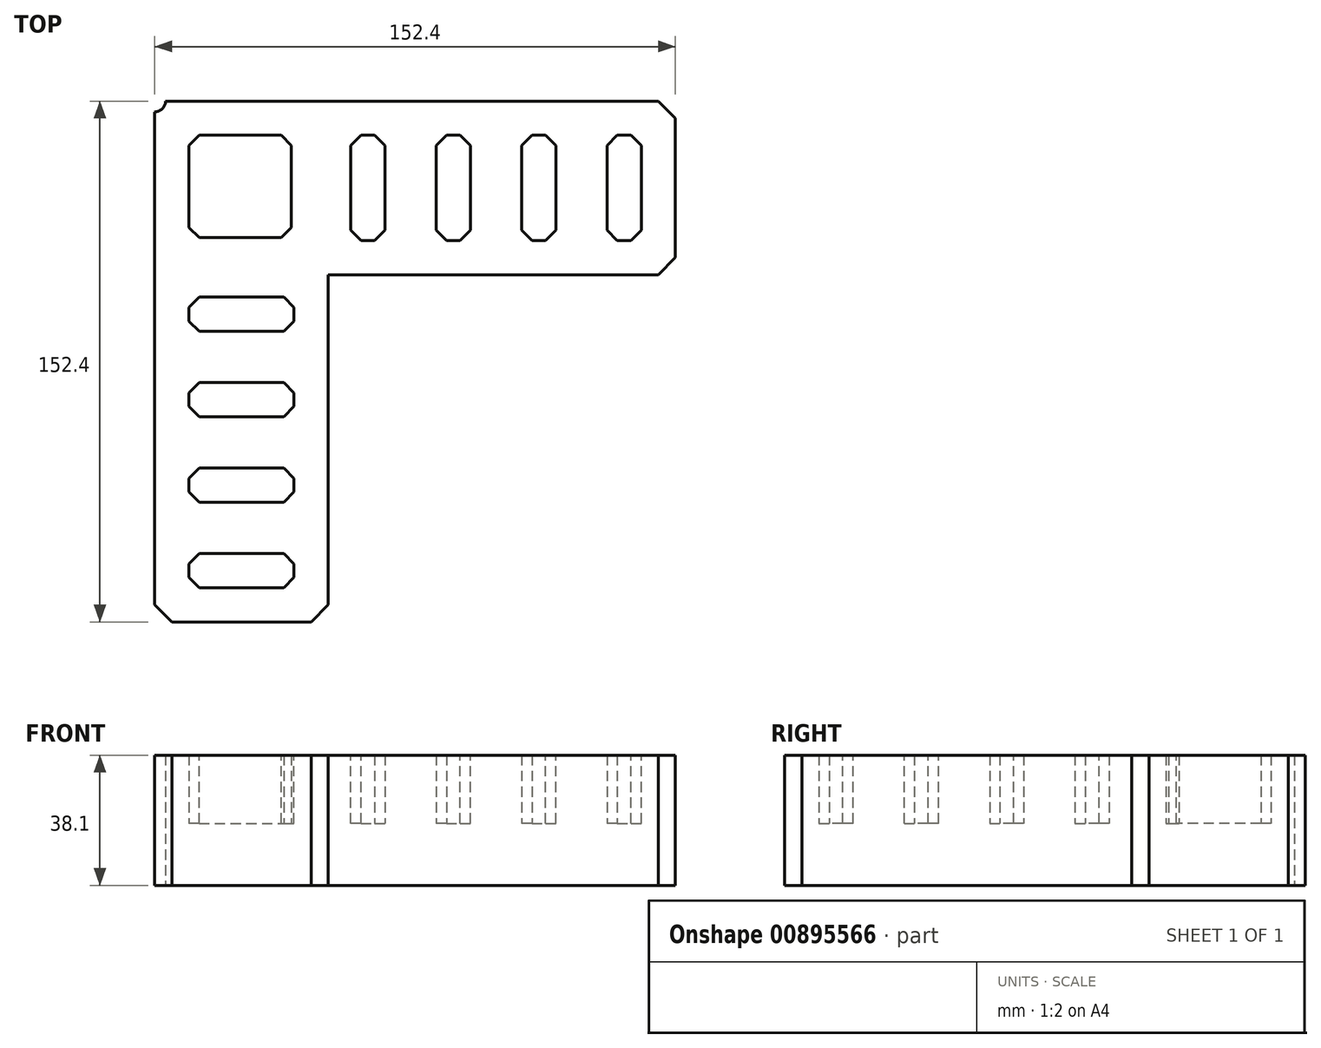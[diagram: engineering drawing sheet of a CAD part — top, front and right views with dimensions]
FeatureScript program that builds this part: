
annotation { "Feature Type Name" : "Feature", "Feature Type Description" : "" }
export const myFeature = defineFeature(function(context is Context, id is Id, definition is map)
    precondition{}
    {
        {
            var Q0;
            Q0=qCreatedBy(makeId("Top.planeOp"),FACE);
            var sketch = newSketch(context, id + "F0", { "sketchPlane" : qUnion([Q0])});
            skLineSegment(sketch, "E0.bottom", {"start": v(0, 0) * mm, "end": v(152.4, 0) * mm});
            skLineSegment(sketch, "E0.top", {"start": v(3.17, 50.8) * mm, "end": v(152.4, 50.8) * mm});
            skLineSegment(sketch, "E0.left", {"start": v(0, 0) * mm, "end": v(0, 47.62) * mm});
            skLineSegment(sketch, "E0.right", {"start": v(152.4, 0) * mm, "end": v(152.4, 50.8) * mm});
            skLineSegment(sketch, "E1.bottom", {"start": v(3.17, 50.8) * mm, "end": v(50.8, 50.8) * mm});
            skLineSegment(sketch, "E1.top", {"start": v(0, -101.6) * mm, "end": v(50.8, -101.6) * mm});
            skLineSegment(sketch, "E1.left", {"start": v(0, 47.62) * mm, "end": v(0, -101.6) * mm});
            skLineSegment(sketch, "E1.right", {"start": v(50.8, 50.8) * mm, "end": v(50.8, -101.6) * mm});
            skArc(sketch, "E2", {"start": v(0, 47.62) * mm, "mid": v(2.25, 48.55) * mm, "end": v(3.17, 50.8) * mm});
            skSolve(sketch);
        }
        {
            var Q0;
            Q0 = qSketchRegion(id + "F0", true);
            extrude(context, id + "F1", {"entities" : qUnion([Q0]), "depth" : 38.1 * mm, "offsetDistance" : 25 * mm});
        }
        {
            var Q0;
            Q0=makeQuery(id+"F1.opExtrude","CAP_FACE",FACE,{"disambiguationData":[OSD([sQuery(id+"F0.wireOp",EDGE,"E0.bottom"),sQuery(id+"F0.wireOp",EDGE,"E0.top"),sQuery(id+"F0.wireOp",EDGE,"E0.right"),sQuery(id+"F0.wireOp",EDGE,"E1.bottom"),sQuery(id+"F0.wireOp",EDGE,"E1.top"),sQuery(id+"F0.wireOp",EDGE,"E1.left"),sQuery(id+"F0.wireOp",EDGE,"E1.right"),sQuery(id+"F0.wireOp",EDGE,"E2")])],"isStart":false});
            var sketch = newSketch(context, id + "F2", { "sketchPlane" : qUnion([Q0])});
            skLineSegment(sketch, "E3.bottom", {"start": v(10, -81.6) * mm, "end": v(40.8, -81.6) * mm});
            skLineSegment(sketch, "E3.top", {"start": v(10, -91.6) * mm, "end": v(40.8, -91.6) * mm});
            skLineSegment(sketch, "E3.left", {"start": v(10, -81.6) * mm, "end": v(10, -91.6) * mm});
            skLineSegment(sketch, "E3.right", {"start": v(40.8, -81.6) * mm, "end": v(40.8, -91.6) * mm});
            skLineSegment(sketch, "E4", {"start": v(50.8, 0) * mm, "end": v(2.25, 48.55) * mm, "construction": true});
            skLineSegment(sketch, "E5.0.1.0", {"start": v(10, -66.6) * mm, "end": v(40.8, -66.6) * mm});
            skLineSegment(sketch, "E5.0.1.1", {"start": v(10, -56.6) * mm, "end": v(10, -66.6) * mm});
            skLineSegment(sketch, "E5.0.1.2", {"start": v(10, -56.6) * mm, "end": v(40.8, -56.6) * mm});
            skLineSegment(sketch, "E5.0.1.3", {"start": v(40.8, -56.6) * mm, "end": v(40.8, -66.6) * mm});
            skLineSegment(sketch, "E5.0.2.0", {"start": v(10, -41.6) * mm, "end": v(40.8, -41.6) * mm});
            skLineSegment(sketch, "E5.0.2.1", {"start": v(10, -31.6) * mm, "end": v(10, -41.6) * mm});
            skLineSegment(sketch, "E5.0.2.2", {"start": v(10, -31.6) * mm, "end": v(40.8, -31.6) * mm});
            skLineSegment(sketch, "E5.0.2.3", {"start": v(40.8, -31.6) * mm, "end": v(40.8, -41.6) * mm});
            skLineSegment(sketch, "E5.0.3.0", {"start": v(10, -16.6) * mm, "end": v(40.8, -16.6) * mm});
            skLineSegment(sketch, "E5.0.3.1", {"start": v(10, -6.6) * mm, "end": v(10, -16.6) * mm});
            skLineSegment(sketch, "E5.0.3.2", {"start": v(10, -6.6) * mm, "end": v(40.8, -6.6) * mm});
            skLineSegment(sketch, "E5.0.3.3", {"start": v(40.8, -6.6) * mm, "end": v(40.8, -16.6) * mm});
            skLineSegment(sketch, "E5.direction1", {"start": v(10, -91.6) * mm, "end": v(35, -91.6) * mm, "construction": true});
            skLineSegment(sketch, "E5.direction2", {"start": v(10, -91.6) * mm, "end": v(10, -66.6) * mm, "construction": true});
            skLineSegment(sketch, "E6.MirrorCS", {"start": v(142.4, 40.8) * mm, "end": v(142.4, 10) * mm});
            skLineSegment(sketch, "E7.MirrorCS", {"start": v(132.4, 40.8) * mm, "end": v(142.4, 40.8) * mm});
            skLineSegment(sketch, "E8.MirrorCS", {"start": v(132.4, 40.8) * mm, "end": v(132.4, 10) * mm});
            skLineSegment(sketch, "E9.MirrorCS", {"start": v(132.4, 10) * mm, "end": v(142.4, 10) * mm});
            skLineSegment(sketch, "E10.MirrorCS", {"start": v(117.4, 40.8) * mm, "end": v(117.4, 10) * mm});
            skLineSegment(sketch, "E11.MirrorCS", {"start": v(107.4, 40.8) * mm, "end": v(117.4, 40.8) * mm});
            skLineSegment(sketch, "E12.MirrorCS", {"start": v(107.4, 40.8) * mm, "end": v(107.4, 10) * mm});
            skLineSegment(sketch, "E13.MirrorCS", {"start": v(107.4, 10) * mm, "end": v(117.4, 10) * mm});
            skLineSegment(sketch, "E14.MirrorCS", {"start": v(92.4, 40.8) * mm, "end": v(92.4, 10) * mm});
            skLineSegment(sketch, "E15.MirrorCS", {"start": v(82.4, 40.8) * mm, "end": v(92.4, 40.8) * mm});
            skLineSegment(sketch, "E16.MirrorCS", {"start": v(142.4, 40.8) * mm, "end": v(142.4, 15.8) * mm, "construction": true});
            skLineSegment(sketch, "E17.MirrorCS", {"start": v(142.4, 40.8) * mm, "end": v(117.4, 40.8) * mm, "construction": true});
            skLineSegment(sketch, "E18.MirrorCS", {"start": v(82.4, 40.8) * mm, "end": v(82.4, 10) * mm});
            skLineSegment(sketch, "E19.MirrorCS", {"start": v(82.4, 10) * mm, "end": v(92.4, 10) * mm});
            skLineSegment(sketch, "E20.MirrorCS", {"start": v(57.4, 10) * mm, "end": v(67.4, 10) * mm});
            skLineSegment(sketch, "E21.MirrorCS", {"start": v(57.4, 40.8) * mm, "end": v(57.4, 10) * mm});
            skLineSegment(sketch, "E22.MirrorCS", {"start": v(67.4, 40.8) * mm, "end": v(67.4, 10) * mm});
            skLineSegment(sketch, "E23.MirrorCS", {"start": v(57.4, 40.8) * mm, "end": v(67.4, 40.8) * mm});
            skLineSegment(sketch, "E24.bottom", {"start": v(10, 40.8) * mm, "end": v(40, 40.8) * mm});
            skLineSegment(sketch, "E24.top", {"start": v(10, 10.8) * mm, "end": v(40, 10.8) * mm});
            skLineSegment(sketch, "E24.left", {"start": v(10, 40.8) * mm, "end": v(10, 10.8) * mm});
            skLineSegment(sketch, "E24.right", {"start": v(40, 40.8) * mm, "end": v(40, 10.8) * mm});
            skSolve(sketch);
        }
        {
            var Q0;
            Q0 = qSketchRegion(id + "F2", true);
            extrude(context, id + "F3", {"entities" : qUnion([Q0]), "operationType" : NewBodyOperationType.REMOVE, "oppositeDirection" : true, "depth" : 20 * mm, "offsetDistance" : 25 * mm});
        }
        {
            var Q0;
            Q0=makeQuery(id+"F3.boolean.opBoolean","COPY",EDGE,{"derivedFrom":makeQuery(id+"F3.opExtrude","SWEPT_EDGE",EDGE,{"disambiguationData":[OSD([sQuery(id+"F2.wireOp",EDGE,"E5.0.3.1"),sQuery(id+"F2.wireOp",EDGE,"E5.0.3.2")])]})});
            var Q1;
            Q1=makeQuery(id+"F3.boolean.opBoolean","COPY",EDGE,{"derivedFrom":makeQuery(id+"F3.opExtrude","SWEPT_EDGE",EDGE,{"disambiguationData":[OSD([sQuery(id+"F2.wireOp",EDGE,"E24.bottom"),sQuery(id+"F2.wireOp",EDGE,"E24.left")])]})});
            var Q2;
            Q2=makeQuery(id+"F3.boolean.opBoolean","COPY",EDGE,{"derivedFrom":makeQuery(id+"F3.opExtrude","SWEPT_EDGE",EDGE,{"disambiguationData":[OSD([sQuery(id+"F2.wireOp",EDGE,"E5.0.2.1"),sQuery(id+"F2.wireOp",EDGE,"E5.0.2.2")])]})});
            var Q3;
            Q3=makeQuery(id+"F3.boolean.opBoolean","COPY",EDGE,{"derivedFrom":makeQuery(id+"F3.opExtrude","SWEPT_EDGE",EDGE,{"disambiguationData":[OSD([sQuery(id+"F2.wireOp",EDGE,"E5.0.1.1"),sQuery(id+"F2.wireOp",EDGE,"E5.0.1.2")])]})});
            var Q4;
            Q4=makeQuery(id+"F3.boolean.opBoolean","COPY",EDGE,{"derivedFrom":makeQuery(id+"F3.opExtrude","SWEPT_EDGE",EDGE,{"disambiguationData":[OSD([sQuery(id+"F2.wireOp",EDGE,"E3.bottom"),sQuery(id+"F2.wireOp",EDGE,"E3.left")])]})});
            var Q5;
            Q5=makeQuery(id+"F3.boolean.opBoolean","COPY",EDGE,{"derivedFrom":makeQuery(id+"F3.opExtrude","SWEPT_EDGE",EDGE,{"disambiguationData":[OSD([sQuery(id+"F2.wireOp",EDGE,"E3.top"),sQuery(id+"F2.wireOp",EDGE,"E3.left")])]})});
            var Q6;
            Q6=makeQuery(id+"F3.boolean.opBoolean","COPY",EDGE,{"derivedFrom":makeQuery(id+"F3.opExtrude","SWEPT_EDGE",EDGE,{"disambiguationData":[OSD([sQuery(id+"F2.wireOp",EDGE,"E3.bottom"),sQuery(id+"F2.wireOp",EDGE,"E3.right")])]})});
            var Q7;
            Q7=makeQuery(id+"F3.boolean.opBoolean","COPY",EDGE,{"derivedFrom":makeQuery(id+"F3.opExtrude","SWEPT_EDGE",EDGE,{"disambiguationData":[OSD([sQuery(id+"F2.wireOp",EDGE,"E3.top"),sQuery(id+"F2.wireOp",EDGE,"E3.right")])]})});
            var Q8;
            Q8=makeQuery(id+"F3.boolean.opBoolean","COPY",EDGE,{"derivedFrom":makeQuery(id+"F3.opExtrude","SWEPT_EDGE",EDGE,{"disambiguationData":[OSD([sQuery(id+"F2.wireOp",EDGE,"E5.0.1.0"),sQuery(id+"F2.wireOp",EDGE,"E5.0.1.3")])]})});
            var Q9;
            Q9=makeQuery(id+"F3.boolean.opBoolean","COPY",EDGE,{"derivedFrom":makeQuery(id+"F3.opExtrude","SWEPT_EDGE",EDGE,{"disambiguationData":[OSD([sQuery(id+"F2.wireOp",EDGE,"E5.0.1.2"),sQuery(id+"F2.wireOp",EDGE,"E5.0.1.3")])]})});
            var Q10;
            Q10=makeQuery(id+"F3.boolean.opBoolean","COPY",EDGE,{"derivedFrom":makeQuery(id+"F3.opExtrude","SWEPT_EDGE",EDGE,{"disambiguationData":[OSD([sQuery(id+"F2.wireOp",EDGE,"E5.0.1.0"),sQuery(id+"F2.wireOp",EDGE,"E5.0.1.1")])]})});
            var Q11;
            Q11=makeQuery(id+"F3.boolean.opBoolean","COPY",EDGE,{"derivedFrom":makeQuery(id+"F3.opExtrude","SWEPT_EDGE",EDGE,{"disambiguationData":[OSD([sQuery(id+"F2.wireOp",EDGE,"E5.0.2.0"),sQuery(id+"F2.wireOp",EDGE,"E5.0.2.1")])]})});
            var Q12;
            Q12=makeQuery(id+"F3.boolean.opBoolean","COPY",EDGE,{"derivedFrom":makeQuery(id+"F3.opExtrude","SWEPT_EDGE",EDGE,{"disambiguationData":[OSD([sQuery(id+"F2.wireOp",EDGE,"E5.0.2.2"),sQuery(id+"F2.wireOp",EDGE,"E5.0.2.3")])]})});
            var Q13;
            Q13=makeQuery(id+"F3.boolean.opBoolean","COPY",EDGE,{"derivedFrom":makeQuery(id+"F3.opExtrude","SWEPT_EDGE",EDGE,{"disambiguationData":[OSD([sQuery(id+"F2.wireOp",EDGE,"E5.0.2.0"),sQuery(id+"F2.wireOp",EDGE,"E5.0.2.3")])]})});
            var Q14;
            Q14=makeQuery(id+"F3.boolean.opBoolean","COPY",EDGE,{"derivedFrom":makeQuery(id+"F3.opExtrude","SWEPT_EDGE",EDGE,{"disambiguationData":[OSD([sQuery(id+"F2.wireOp",EDGE,"E5.0.3.0"),sQuery(id+"F2.wireOp",EDGE,"E5.0.3.1")])]})});
            var Q15;
            Q15=makeQuery(id+"F3.boolean.opBoolean","COPY",EDGE,{"derivedFrom":makeQuery(id+"F3.opExtrude","SWEPT_EDGE",EDGE,{"disambiguationData":[OSD([sQuery(id+"F2.wireOp",EDGE,"E5.0.3.0"),sQuery(id+"F2.wireOp",EDGE,"E5.0.3.3")])]})});
            var Q16;
            Q16=makeQuery(id+"F3.boolean.opBoolean","COPY",EDGE,{"derivedFrom":makeQuery(id+"F3.opExtrude","SWEPT_EDGE",EDGE,{"disambiguationData":[OSD([sQuery(id+"F2.wireOp",EDGE,"E5.0.3.2"),sQuery(id+"F2.wireOp",EDGE,"E5.0.3.3")])]})});
            var Q17;
            Q17=makeQuery(id+"F3.boolean.opBoolean","COPY",EDGE,{"derivedFrom":makeQuery(id+"F3.opExtrude","SWEPT_EDGE",EDGE,{"disambiguationData":[OSD([sQuery(id+"F2.wireOp",EDGE,"E24.top"),sQuery(id+"F2.wireOp",EDGE,"E24.left")])]})});
            var Q18;
            Q18=makeQuery(id+"F3.boolean.opBoolean","COPY",EDGE,{"derivedFrom":makeQuery(id+"F3.opExtrude","SWEPT_EDGE",EDGE,{"disambiguationData":[OSD([sQuery(id+"F2.wireOp",EDGE,"E24.bottom"),sQuery(id+"F2.wireOp",EDGE,"E24.right")])]})});
            var Q19;
            Q19=makeQuery(id+"F3.boolean.opBoolean","COPY",EDGE,{"derivedFrom":makeQuery(id+"F3.opExtrude","SWEPT_EDGE",EDGE,{"disambiguationData":[OSD([sQuery(id+"F2.wireOp",EDGE,"E24.top"),sQuery(id+"F2.wireOp",EDGE,"E24.right")])]})});
            var Q20;
            Q20=makeQuery(id+"F3.boolean.opBoolean","COPY",EDGE,{"derivedFrom":makeQuery(id+"F3.opExtrude","SWEPT_EDGE",EDGE,{"disambiguationData":[OSD([sQuery(id+"F2.wireOp",EDGE,"E21.MirrorCS"),sQuery(id+"F2.wireOp",EDGE,"E23.MirrorCS")])]})});
            var Q21;
            Q21=makeQuery(id+"F3.boolean.opBoolean","COPY",EDGE,{"derivedFrom":makeQuery(id+"F3.opExtrude","SWEPT_EDGE",EDGE,{"disambiguationData":[OSD([sQuery(id+"F2.wireOp",EDGE,"E20.MirrorCS"),sQuery(id+"F2.wireOp",EDGE,"E21.MirrorCS")])]})});
            var Q22;
            Q22=makeQuery(id+"F3.boolean.opBoolean","COPY",EDGE,{"derivedFrom":makeQuery(id+"F3.opExtrude","SWEPT_EDGE",EDGE,{"disambiguationData":[OSD([sQuery(id+"F2.wireOp",EDGE,"E20.MirrorCS"),sQuery(id+"F2.wireOp",EDGE,"E22.MirrorCS")])]})});
            var Q23;
            Q23=makeQuery(id+"F3.boolean.opBoolean","COPY",EDGE,{"derivedFrom":makeQuery(id+"F3.opExtrude","SWEPT_EDGE",EDGE,{"disambiguationData":[OSD([sQuery(id+"F2.wireOp",EDGE,"E22.MirrorCS"),sQuery(id+"F2.wireOp",EDGE,"E23.MirrorCS")])]})});
            var Q24;
            Q24=makeQuery(id+"F3.boolean.opBoolean","COPY",EDGE,{"derivedFrom":makeQuery(id+"F3.opExtrude","SWEPT_EDGE",EDGE,{"disambiguationData":[OSD([sQuery(id+"F2.wireOp",EDGE,"E15.MirrorCS"),sQuery(id+"F2.wireOp",EDGE,"E18.MirrorCS")])]})});
            var Q25;
            Q25=makeQuery(id+"F3.boolean.opBoolean","COPY",EDGE,{"derivedFrom":makeQuery(id+"F3.opExtrude","SWEPT_EDGE",EDGE,{"disambiguationData":[OSD([sQuery(id+"F2.wireOp",EDGE,"E18.MirrorCS"),sQuery(id+"F2.wireOp",EDGE,"E19.MirrorCS")])]})});
            var Q26;
            Q26=makeQuery(id+"F3.boolean.opBoolean","COPY",EDGE,{"derivedFrom":makeQuery(id+"F3.opExtrude","SWEPT_EDGE",EDGE,{"disambiguationData":[OSD([sQuery(id+"F2.wireOp",EDGE,"E14.MirrorCS"),sQuery(id+"F2.wireOp",EDGE,"E15.MirrorCS")])]})});
            var Q27;
            Q27=makeQuery(id+"F3.boolean.opBoolean","COPY",EDGE,{"derivedFrom":makeQuery(id+"F3.opExtrude","SWEPT_EDGE",EDGE,{"disambiguationData":[OSD([sQuery(id+"F2.wireOp",EDGE,"E14.MirrorCS"),sQuery(id+"F2.wireOp",EDGE,"E19.MirrorCS")])]})});
            var Q28;
            Q28=makeQuery(id+"F3.boolean.opBoolean","COPY",EDGE,{"derivedFrom":makeQuery(id+"F3.opExtrude","SWEPT_EDGE",EDGE,{"disambiguationData":[OSD([sQuery(id+"F2.wireOp",EDGE,"E12.MirrorCS"),sQuery(id+"F2.wireOp",EDGE,"E13.MirrorCS")])]})});
            var Q29;
            Q29=makeQuery(id+"F3.boolean.opBoolean","COPY",EDGE,{"derivedFrom":makeQuery(id+"F3.opExtrude","SWEPT_EDGE",EDGE,{"disambiguationData":[OSD([sQuery(id+"F2.wireOp",EDGE,"E10.MirrorCS"),sQuery(id+"F2.wireOp",EDGE,"E13.MirrorCS")])]})});
            var Q30;
            Q30=makeQuery(id+"F3.boolean.opBoolean","COPY",EDGE,{"derivedFrom":makeQuery(id+"F3.opExtrude","SWEPT_EDGE",EDGE,{"disambiguationData":[OSD([sQuery(id+"F2.wireOp",EDGE,"E10.MirrorCS"),sQuery(id+"F2.wireOp",EDGE,"E11.MirrorCS")])]})});
            var Q31;
            Q31=makeQuery(id+"F3.boolean.opBoolean","COPY",EDGE,{"derivedFrom":makeQuery(id+"F3.opExtrude","SWEPT_EDGE",EDGE,{"disambiguationData":[OSD([sQuery(id+"F2.wireOp",EDGE,"E11.MirrorCS"),sQuery(id+"F2.wireOp",EDGE,"E12.MirrorCS")])]})});
            var Q32;
            Q32=makeQuery(id+"F3.boolean.opBoolean","COPY",EDGE,{"derivedFrom":makeQuery(id+"F3.opExtrude","SWEPT_EDGE",EDGE,{"disambiguationData":[OSD([sQuery(id+"F2.wireOp",EDGE,"E8.MirrorCS"),sQuery(id+"F2.wireOp",EDGE,"E9.MirrorCS")])]})});
            var Q33;
            Q33=makeQuery(id+"F3.boolean.opBoolean","COPY",EDGE,{"derivedFrom":makeQuery(id+"F3.opExtrude","SWEPT_EDGE",EDGE,{"disambiguationData":[OSD([sQuery(id+"F2.wireOp",EDGE,"E6.MirrorCS"),sQuery(id+"F2.wireOp",EDGE,"E9.MirrorCS")])]})});
            var Q34;
            Q34=makeQuery(id+"F3.boolean.opBoolean","COPY",EDGE,{"derivedFrom":makeQuery(id+"F3.opExtrude","SWEPT_EDGE",EDGE,{"disambiguationData":[OSD([sQuery(id+"F2.wireOp",EDGE,"E6.MirrorCS"),sQuery(id+"F2.wireOp",EDGE,"E7.MirrorCS")])]})});
            var Q35;
            Q35=makeQuery(id+"F3.boolean.opBoolean","COPY",EDGE,{"derivedFrom":makeQuery(id+"F3.opExtrude","SWEPT_EDGE",EDGE,{"disambiguationData":[OSD([sQuery(id+"F2.wireOp",EDGE,"E7.MirrorCS"),sQuery(id+"F2.wireOp",EDGE,"E8.MirrorCS")])]})});
            chamfer(context, id + "F4", {"entities" : qUnion([Q0, Q1, Q2, Q3, Q4, Q5, Q6, Q7, Q8, Q9, Q10, Q11, Q12, Q13, Q14, Q15, Q16, Q17, Q18, Q19, Q20, Q21, Q22, Q23, Q24, Q25, Q26, Q27, Q28, Q29, Q30, Q31, Q32, Q33, Q34, Q35]), "width" : 3 * mm, "tangentPropagation" : true});
        }
        {
            var Q0;
            Q0=makeQuery(id+"F1.opExtrude","SWEPT_EDGE",EDGE,{"disambiguationData":[OSD([sQuery(id+"F0.wireOp",EDGE,"E1.top"),sQuery(id+"F0.wireOp",EDGE,"E1.left")])]});
            var Q1;
            Q1=makeQuery(id+"F1.opExtrude","SWEPT_EDGE",EDGE,{"disambiguationData":[OSD([sQuery(id+"F0.wireOp",EDGE,"E1.top"),sQuery(id+"F0.wireOp",EDGE,"E1.right")])]});
            var Q2;
            Q2=makeQuery(id+"F1.opExtrude","SWEPT_EDGE",EDGE,{"disambiguationData":[OSD([sQuery(id+"F0.wireOp",EDGE,"E0.bottom"),sQuery(id+"F0.wireOp",EDGE,"E0.right")])]});
            var Q3;
            Q3=makeQuery(id+"F1.opExtrude","SWEPT_EDGE",EDGE,{"disambiguationData":[OSD([sQuery(id+"F0.wireOp",EDGE,"E0.top"),sQuery(id+"F0.wireOp",EDGE,"E0.right")])]});
            chamfer(context, id + "F5", {"entities" : qUnion([Q0, Q1, Q2, Q3]), "width" : 5 * mm, "tangentPropagation" : true});
        }
    });
